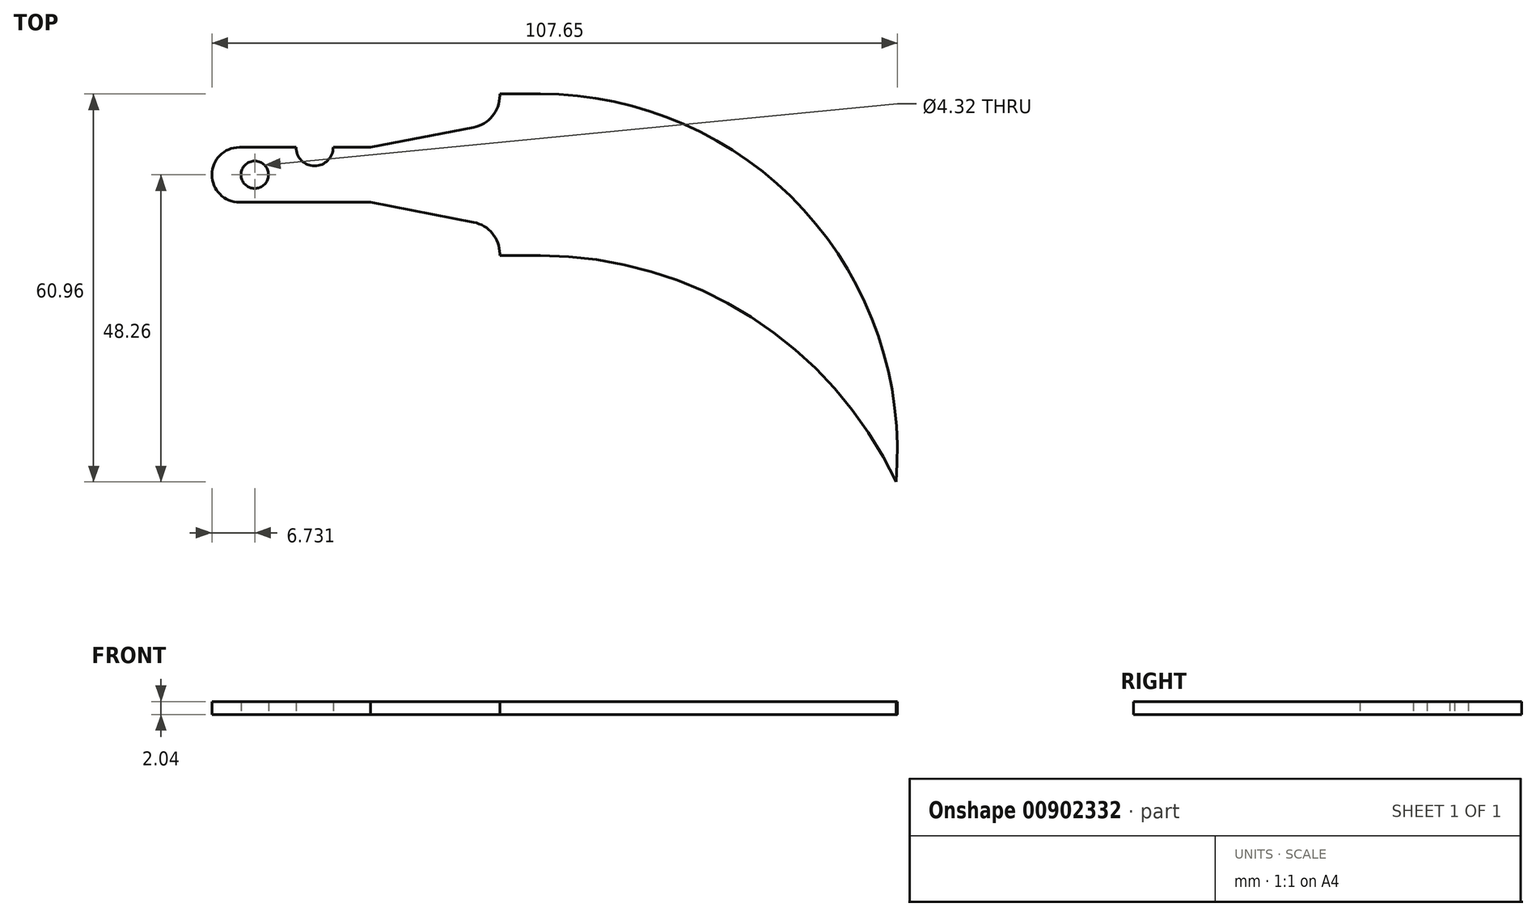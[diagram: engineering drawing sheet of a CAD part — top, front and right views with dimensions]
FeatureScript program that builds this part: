
annotation { "Feature Type Name" : "Feature", "Feature Type Description" : "" }
export const myFeature = defineFeature(function(context is Context, id is Id, definition is map)
    precondition{}
    {
        {
            var Q0;
            Q0=qCreatedBy(makeId("Top.planeOp"),FACE);
            var sketch = newSketch(context, id + "F0", { "sketchPlane" : qUnion([Q0])});
            skArc(sketch, "E0", {"start": v(4.32, 22.1) * mm, "mid": v(0, 17.78) * mm, "end": v(4.32, 13.46) * mm});
            skCircle(sketch, "E1", {"center": v(6.73, 17.78) * mm, "radius": 2.16 * mm});
            skLineSegment(sketch, "E2", {"start": v(4.32, 22.1) * mm, "end": v(13.2, 22.1) * mm});
            skLineSegment(sketch, "E3", {"start": v(24.9, 22.1) * mm, "end": v(24.9, 13.46) * mm, "construction": true});
            skPoint(sketch, "E4", {"position": v(0, 17.78) * mm});
            skPoint(sketch, "E5", {"position": v(4.57, 17.78) * mm});
            skLineSegment(sketch, "E6", {"start": v(24.9, 22.1) * mm, "end": v(41.1, 25.24) * mm});
            skLineSegment(sketch, "E7", {"start": v(45.21, 30.23) * mm, "end": v(45.21, 30.48) * mm});
            skLineSegment(sketch, "E8", {"start": v(45.21, 30.48) * mm, "end": v(51.56, 30.48) * mm});
            skLineSegment(sketch, "E9", {"start": v(51.56, 30.48) * mm, "end": v(51.56, 5.08) * mm, "construction": true});
            skLineSegment(sketch, "E10", {"start": v(51.56, 5.08) * mm, "end": v(45.21, 5.08) * mm});
            skLineSegment(sketch, "E11", {"start": v(45.21, 5.08) * mm, "end": v(45.21, 5.33) * mm});
            skLineSegment(sketch, "E12", {"start": v(41.1, 10.32) * mm, "end": v(24.9, 13.46) * mm});
            skPoint(sketch, "E13.visualSharp", {"position": v(45.21, 9.52) * mm});
            skArc(sketch, "E13.filletArc", {"start": v(45.21, 5.33) * mm, "mid": v(44.05, 8.57) * mm, "end": v(41.1, 10.32) * mm});
            skPoint(sketch, "E14.visualSharp", {"position": v(45.21, 26.04) * mm});
            skArc(sketch, "E14.filletArc", {"start": v(41.1, 25.24) * mm, "mid": v(44.05, 27) * mm, "end": v(45.21, 30.23) * mm});
            skArc(sketch, "E15", {"start": v(107.44, -30.48) * mm, "mid": v(84.68, -4.56) * mm, "end": v(51.56, 5.08) * mm});
            skArc(sketch, "E16", {"start": v(107.44, -30.48) * mm, "mid": v(92.91, 12.3) * mm, "end": v(51.56, 30.48) * mm});
            skLineSegment(sketch, "E17", {"start": v(0, 17.78) * mm, "end": v(51.56, 17.78) * mm, "construction": true});
            skArc(sketch, "E18", {"start": v(13.2, 22.1) * mm, "mid": v(16.13, 19.18) * mm, "end": v(19.05, 22.1) * mm});
            skLineSegment(sketch, "E19.trimOffspring", {"start": v(19.05, 22.1) * mm, "end": v(24.9, 22.1) * mm});
            skLineSegment(sketch, "E20", {"start": v(4.32, 13.46) * mm, "end": v(24.9, 13.46) * mm});
            skSolve(sketch);
        }
        {
            var Q0;
            Q0 = qSketchRegion(id + "F0", true);
            extrude(context, id + "F1", {"entities" : qUnion([Q0]), "endBound" : BoundingType.SYMMETRIC, "depth" : 2.03 * mm, "offsetDistance" : 25.4 * mm});
        }
    });
